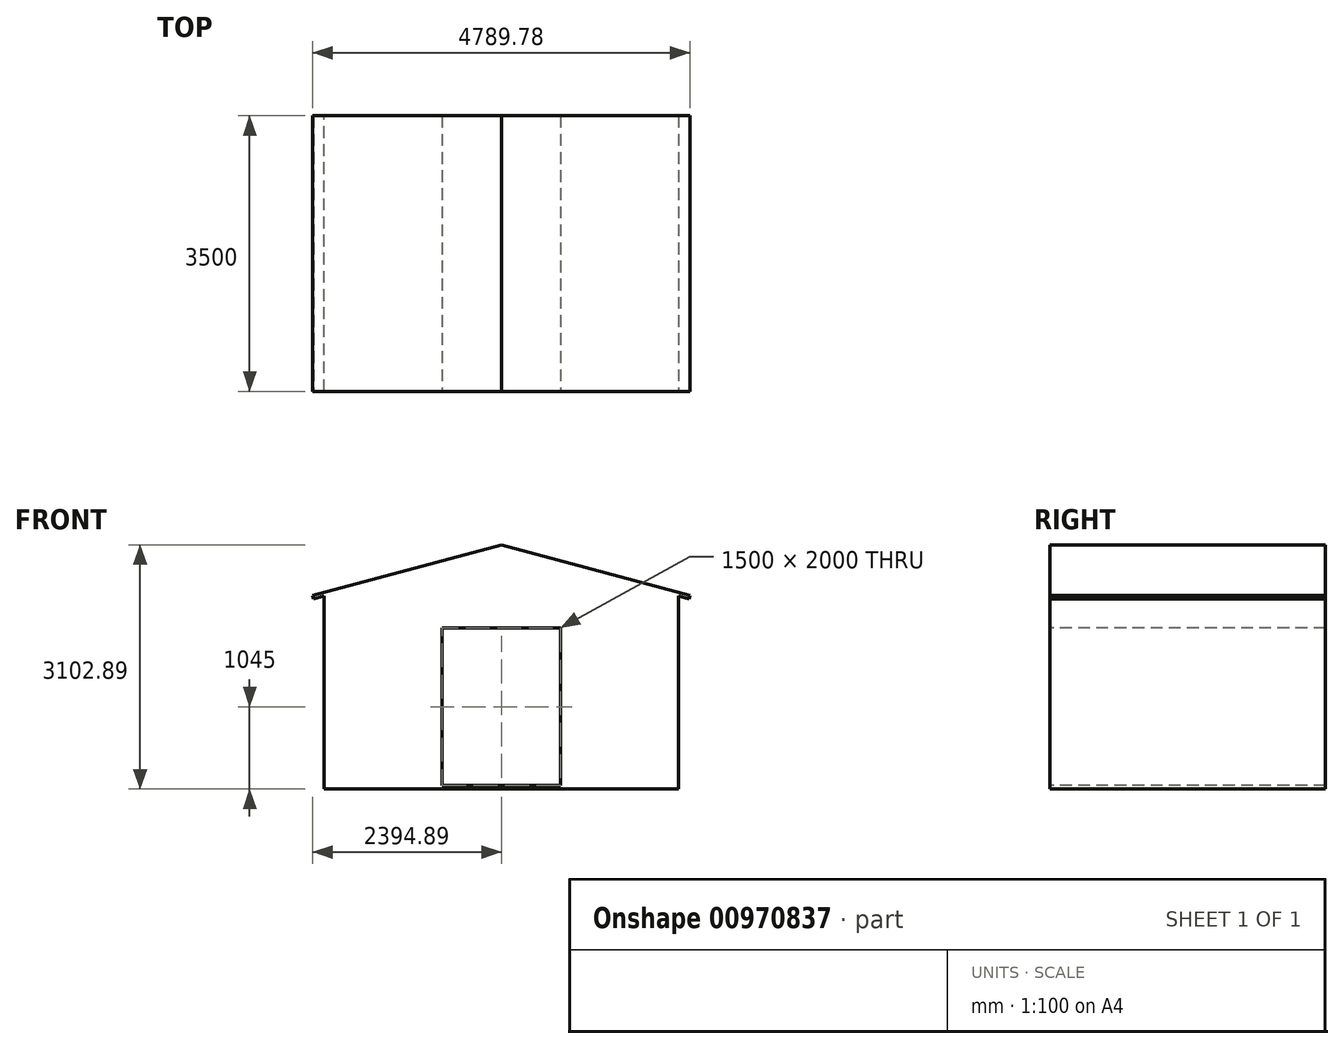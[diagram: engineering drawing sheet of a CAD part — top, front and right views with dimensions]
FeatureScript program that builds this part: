
annotation { "Feature Type Name" : "Feature", "Feature Type Description" : "" }
export const myFeature = defineFeature(function(context is Context, id is Id, definition is map)
    precondition{}
    {
        {
            var Q0;
            Q0=qCreatedBy(makeId("Front.planeOp"),FACE);
            var sketch = newSketch(context, id + "F0", { "sketchPlane" : qUnion([Q0])});
            skLineSegment(sketch, "E0.top", {"start": v(-2250, 0) * mm, "end": v(2250, 0) * mm});
            skLineSegment(sketch, "E0.left", {"start": v(-2250, 2500) * mm, "end": v(-2250, 0) * mm});
            skLineSegment(sketch, "E0.right", {"start": v(2250, 2500) * mm, "end": v(2250, 0) * mm});
            skLineSegment(sketch, "E1", {"start": v(-2250, 2500) * mm, "end": v(0, 3102.89) * mm});
            skLineSegment(sketch, "E2", {"start": v(0, 3102.89) * mm, "end": v(2250, 2500) * mm});
            skLineSegment(sketch, "E3", {"start": v(0, 3102.89) * mm, "end": v(0, 0) * mm, "construction": true});
            skLineSegment(sketch, "E4", {"start": v(-2250, 2500) * mm, "end": v(2250, 2500) * mm, "construction": true});
            skSolve(sketch);
        }
        {
            var Q0;
            Q0 = qSketchRegion(id + "F0", true);
            extrude(context, id + "F1", {"entities" : qUnion([Q0]), "endBound" : BoundingType.SYMMETRIC, "depth" : 3500 * mm, "offsetDistance" : 25 * mm});
        }
        {
            var Q0;
            Q0=makeQuery(id+"F1.opExtrude","CAP_FACE",FACE,{"disambiguationData":[OSD([sQuery(id+"F0.wireOp",EDGE,"E0.bottom"),sQuery(id+"F0.wireOp",EDGE,"E0.top"),sQuery(id+"F0.wireOp",EDGE,"E0.left"),sQuery(id+"F0.wireOp",EDGE,"E0.right")])],"isStart":false});
            var sketch = newSketch(context, id + "F2", { "sketchPlane" : qUnion([Q0])});
            skLineSegment(sketch, "E5.bottom", {"start": v(-750, 2045) * mm, "end": v(750, 2045) * mm});
            skLineSegment(sketch, "E5.top", {"start": v(-750, 45) * mm, "end": v(750, 45) * mm});
            skLineSegment(sketch, "E5.left", {"start": v(-750, 2045) * mm, "end": v(-750, 45) * mm});
            skLineSegment(sketch, "E5.right", {"start": v(750, 2045) * mm, "end": v(750, 45) * mm});
            skLineSegment(sketch, "E6", {"start": v(0, 0) * mm, "end": v(0, 45) * mm, "construction": true});
            skSolve(sketch);
        }
        {
            var Q0;
            Q0 = qSketchRegion(id + "F2", true);
            extrude(context, id + "F3", {"entities" : qUnion([Q0]), "operationType" : NewBodyOperationType.REMOVE, "endBound" : BoundingType.UP_TO_NEXT, "oppositeDirection" : true, "depth" : 25 * mm, "offsetDistance" : 25 * mm});
        }
        {
            var Q0;
            Q0=makeQuery(id+"F1.opExtrude","CAP_FACE",FACE,{"disambiguationData":[OSD([sQuery(id+"F0.wireOp",EDGE,"E0.top"),sQuery(id+"F0.wireOp",EDGE,"E0.left"),sQuery(id+"F0.wireOp",EDGE,"E0.right"),sQuery(id+"F0.wireOp",EDGE,"E1"),sQuery(id+"F0.wireOp",EDGE,"E2")])],"isStart":false});
            var sketch = newSketch(context, id + "F4", { "sketchPlane" : qUnion([Q0])});
            skLineSegment(sketch, "E7", {"start": v(0, 3102.89) * mm, "end": v(0, -958.27) * mm});
            skLineSegment(sketch, "E8", {"start": v(0, 3102.89) * mm, "end": v(-2738.41, 3102.89) * mm});
            skLineSegment(sketch, "E9", {"start": v(-2738.41, 3102.89) * mm, "end": v(-2852.3, -958.27) * mm});
            skLineSegment(sketch, "E10", {"start": v(-2852.3, -958.27) * mm, "end": v(0, -958.27) * mm});
            skSolve(sketch);
        }
        {
            var Q0;
            Q0 = qSketchRegion(id + "F4", true);
            extrude(context, id + "F5", {"entities" : qUnion([Q0]), "operationType" : NewBodyOperationType.REMOVE, "endBound" : BoundingType.THROUGH_ALL, "oppositeDirection" : true, "depth" : 25 * mm, "offsetDistance" : 25 * mm});
        }
        {
            var Q0;
            Q0=makeQuery(id+"F1.opExtrude","CAP_FACE",FACE,{"disambiguationData":[OSD([sQuery(id+"F0.wireOp",EDGE,"E0.top"),sQuery(id+"F0.wireOp",EDGE,"E0.left"),sQuery(id+"F0.wireOp",EDGE,"E0.right"),sQuery(id+"F0.wireOp",EDGE,"E1"),sQuery(id+"F0.wireOp",EDGE,"E2")])],"isStart":false});
            var sketch = newSketch(context, id + "F6", { "sketchPlane" : qUnion([Q0])});
            skLineSegment(sketch, "E11", {"start": v(2250, 2500) * mm, "end": v(2394.89, 2461.18) * mm});
            skLineSegment(sketch, "E12", {"start": v(2394.89, 2461.18) * mm, "end": v(2383.24, 2417.71) * mm});
            skLineSegment(sketch, "E13", {"start": v(2383.24, 2417.71) * mm, "end": v(2238.35, 2456.53) * mm});
            skLineSegment(sketch, "E14", {"start": v(2238.35, 2456.53) * mm, "end": v(2250, 2500) * mm});
            skSolve(sketch);
        }
        {
            var Q0;
            Q0 = qSketchRegion(id + "F6", true);
            extrude(context, id + "F7", {"entities" : qUnion([Q0]), "operationType" : NewBodyOperationType.ADD, "oppositeDirection" : true, "depth" : 3500 * mm, "offsetDistance" : 25 * mm});
        }
        {
            var Q0;
            Q0=makeQuery(id+"F1.opExtrude","SWEPT_BODY",BODY,{"disambiguationData":[OSD([sQuery(id+"F0.wireOp",EDGE,"E0.top"),sQuery(id+"F0.wireOp",EDGE,"E0.left"),sQuery(id+"F0.wireOp",EDGE,"E0.right"),sQuery(id+"F0.wireOp",EDGE,"E1"),sQuery(id+"F0.wireOp",EDGE,"E2")])]});
            var Q1;
            Q1=qCreatedBy(makeId("Right.planeOp"),FACE);
            mirror(context, id + "F8", {"operationType" : NewBodyOperationType.ADD, "entities" : qUnion([Q0]), "mirrorPlane" : qUnion([Q1])});
        }
    });
